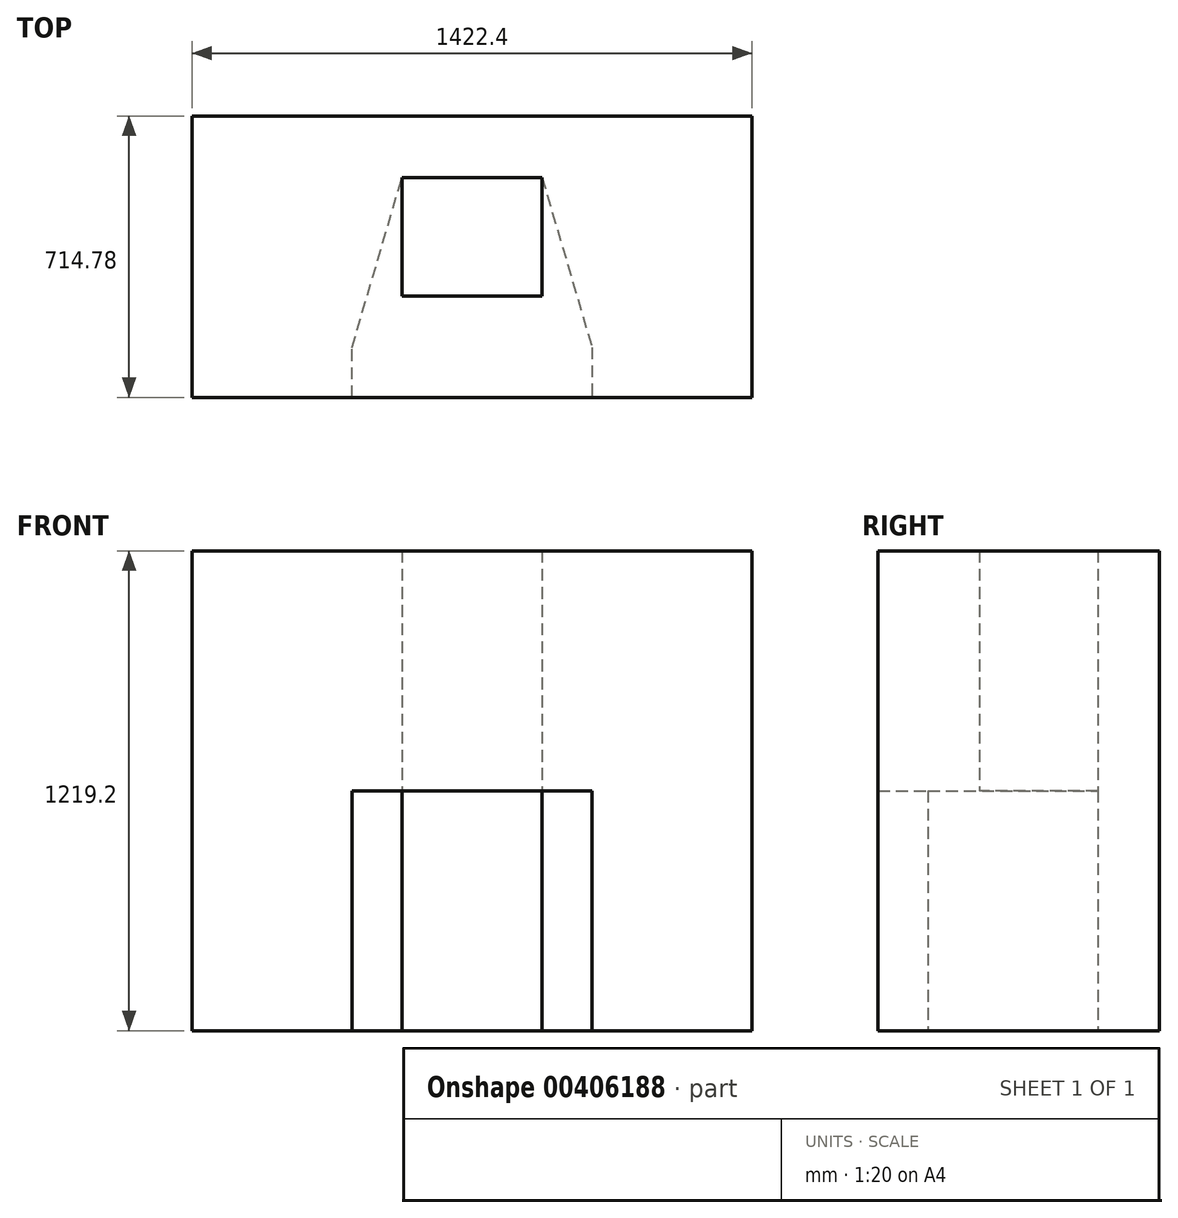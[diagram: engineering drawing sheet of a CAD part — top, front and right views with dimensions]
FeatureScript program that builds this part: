
annotation { "Feature Type Name" : "Feature", "Feature Type Description" : "" }
export const myFeature = defineFeature(function(context is Context, id is Id, definition is map)
    precondition{}
    {
        {
            var Q0;
            Q0=qCreatedBy(makeId("Top.planeOp"),FACE);
            var sketch = newSketch(context, id + "F0", { "sketchPlane" : qUnion([Q0])});
            skLineSegment(sketch, "E0", {"start": v(-304.8, 0) * mm, "end": v(-304.8, 127) * mm});
            skLineSegment(sketch, "E1", {"start": v(-304.8, 127) * mm, "end": v(-177.8, 558.8) * mm});
            skLineSegment(sketch, "E2", {"start": v(-177.8, 558.8) * mm, "end": v(177.8, 558.8) * mm});
            skLineSegment(sketch, "E3", {"start": v(177.8, 558.8) * mm, "end": v(304.8, 127) * mm});
            skLineSegment(sketch, "E4", {"start": v(304.8, 127) * mm, "end": v(304.8, 0) * mm});
            skLineSegment(sketch, "E5", {"start": v(304.8, 0) * mm, "end": v(711.2, 0) * mm});
            skLineSegment(sketch, "E6", {"start": v(711.2, 0) * mm, "end": v(711.2, 714.78) * mm});
            skLineSegment(sketch, "E7", {"start": v(-711.2, 714.78) * mm, "end": v(-711.2, 0) * mm});
            skLineSegment(sketch, "E8", {"start": v(-711.2, 0) * mm, "end": v(-304.8, 0) * mm});
            skLineSegment(sketch, "E9", {"start": v(-711.2, 714.78) * mm, "end": v(711.2, 714.78) * mm});
            skLineSegment(sketch, "E10", {"start": v(0, 0) * mm, "end": v(0, 558.8) * mm, "construction": true});
            skLineSegment(sketch, "E11", {"start": v(-304.8, 0) * mm, "end": v(304.8, 0) * mm, "construction": true});
            skSolve(sketch);
        }
        {
            var Q0;
            Q0=makeQuery(id+"F0.imprint","IMPRINT",FACE,{"disambiguationData":[TD([[makeQuery(id+"F0.imprint","IMPRINT",EDGE,{"derivedFrom":sQuery(id+"F0.wireOp",EDGE,"E0")}),1.0]])]});
            extrude(context, id + "F1", {"entities" : qUnion([Q0]), "depth" : 609.6 * mm});
        }
        {
            var Q0;
            Q0=makeQuery(id+"F1.opExtrude","CAP_FACE",FACE,{"disambiguationData":[OSD([sQuery(id+"F0.wireOp",EDGE,"E0"),sQuery(id+"F0.wireOp",EDGE,"E1"),sQuery(id+"F0.wireOp",EDGE,"E2"),sQuery(id+"F0.wireOp",EDGE,"E3"),sQuery(id+"F0.wireOp",EDGE,"E4"),sQuery(id+"F0.wireOp",EDGE,"E5"),sQuery(id+"F0.wireOp",EDGE,"E6"),sQuery(id+"F0.wireOp",EDGE,"E7"),sQuery(id+"F0.wireOp",EDGE,"E8"),sQuery(id+"F0.wireOp",EDGE,"E9")])],"isStart":false});
            var sketch = newSketch(context, id + "F2", { "sketchPlane" : qUnion([Q0])});
            skLineSegment(sketch, "E12.bottom", {"start": v(-711.2, 714.78) * mm, "end": v(711.2, 714.78) * mm});
            skLineSegment(sketch, "E12.top", {"start": v(-711.2, 0) * mm, "end": v(711.2, 0) * mm});
            skLineSegment(sketch, "E12.left", {"start": v(-711.2, 714.78) * mm, "end": v(-711.2, 0) * mm});
            skLineSegment(sketch, "E12.right", {"start": v(711.2, 714.78) * mm, "end": v(711.2, 0) * mm});
            skLineSegment(sketch, "E13.bottom", {"start": v(-177.8, 558.8) * mm, "end": v(177.8, 558.8) * mm});
            skLineSegment(sketch, "E13.top", {"start": v(-177.8, 257.34) * mm, "end": v(177.8, 257.34) * mm});
            skLineSegment(sketch, "E13.left", {"start": v(-177.8, 558.8) * mm, "end": v(-177.8, 257.34) * mm});
            skLineSegment(sketch, "E13.right", {"start": v(177.8, 558.8) * mm, "end": v(177.8, 257.34) * mm});
            skSolve(sketch);
        }
        {
            var Q0;
            Q0=makeQuery(id+"F2.imprint","IMPRINT",FACE,{"disambiguationData":[TD([[makeQuery(id+"F2.imprint","IMPRINT",EDGE,{"derivedFrom":sQuery(id+"F2.wireOp",EDGE,"E12.bottom")}),-1.0]])]});
            var Q1;
            {var subQ0=makeQuery(id+"F1.opExtrude","CAP_EDGE",EDGE,{"disambiguationData":[OSD([sQuery(id+"F0.wireOp",EDGE,"E0")])],"isStart":false});Q1=makeQuery(id+"F2.imprint","IMPRINT",FACE,{"disambiguationData":[TD([[makeQuery(id+"F2.imprint","IMPRINT",EDGE,{"derivedFrom":subQ0}),-1.0]])]});}
            extrude(context, id + "F3", {"entities" : qUnion([Q0, Q1]), "operationType" : NewBodyOperationType.ADD, "depth" : 609.6 * mm});
        }
    });
